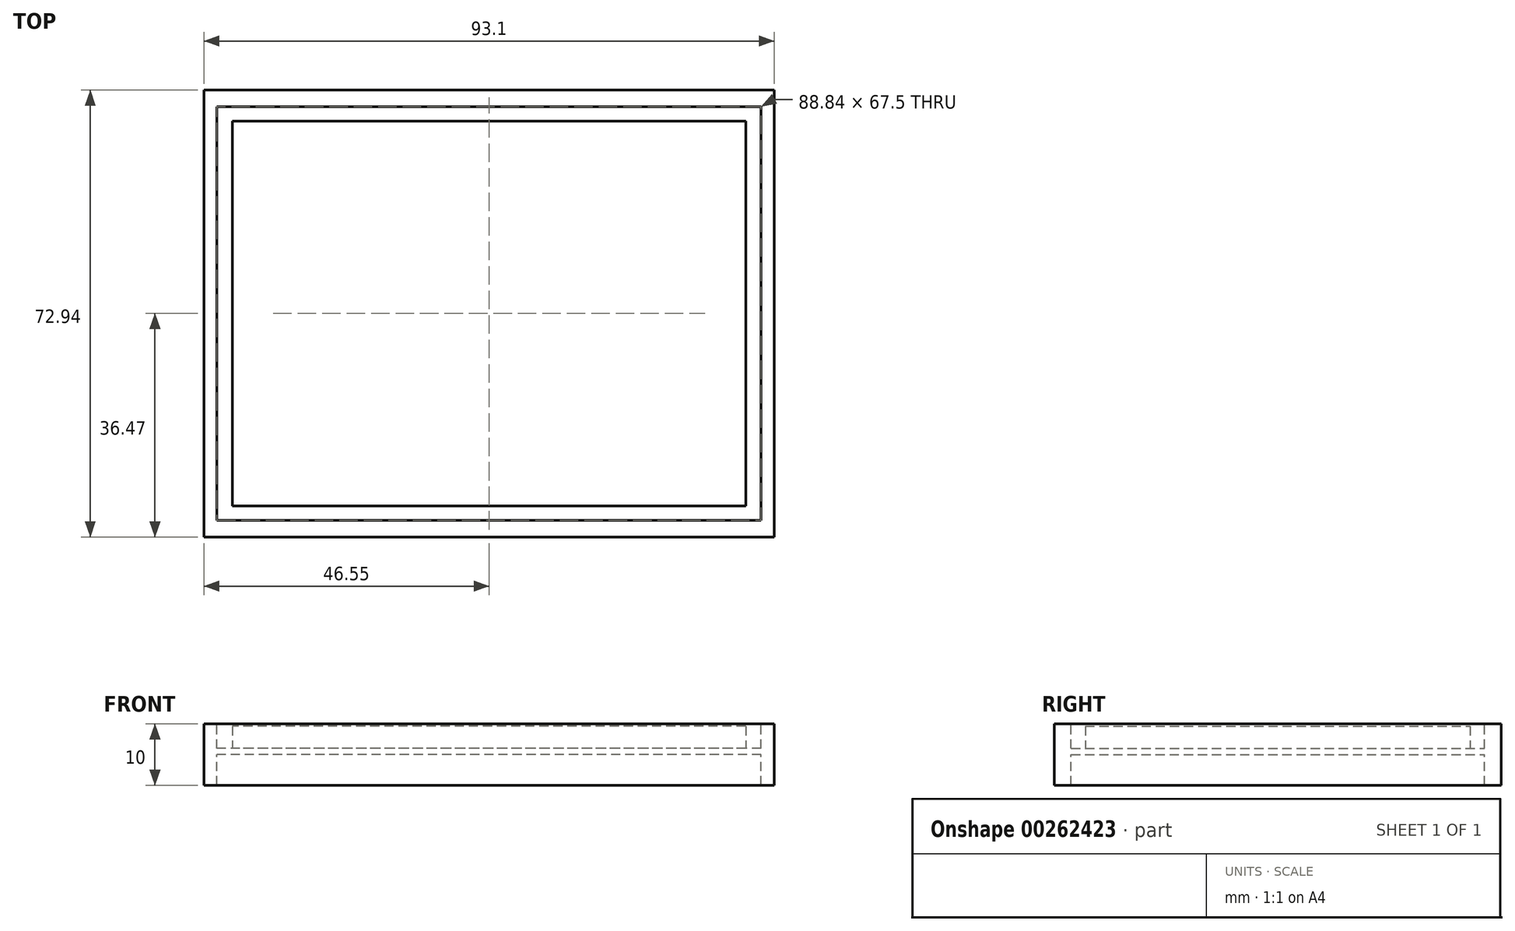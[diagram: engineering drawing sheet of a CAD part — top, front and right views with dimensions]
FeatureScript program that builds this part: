
annotation { "Feature Type Name" : "Feature", "Feature Type Description" : "" }
export const myFeature = defineFeature(function(context is Context, id is Id, definition is map)
    precondition{}
    {
        {
            var Q0;
            Q0=qCreatedBy(makeId("Top.planeOp"),FACE);
            var sketch = newSketch(context, id + "F0", { "sketchPlane" : qUnion([Q0])});
            skLineSegment(sketch, "E0.bottom", {"start": v(46.55, 36.47) * mm, "end": v(-46.55, 36.47) * mm});
            skLineSegment(sketch, "E0.top", {"start": v(46.55, -36.47) * mm, "end": v(-46.55, -36.47) * mm});
            skLineSegment(sketch, "E0.left", {"start": v(46.55, 36.47) * mm, "end": v(46.55, -36.47) * mm});
            skLineSegment(sketch, "E0.right", {"start": v(-46.55, 36.47) * mm, "end": v(-46.55, -36.47) * mm});
            skPoint(sketch, "E0.middle", {"position": v(0, 0) * mm});
            skLineSegment(sketch, "E1.bottom", {"start": v(41.9, -31.42) * mm, "end": v(-41.9, -31.42) * mm});
            skLineSegment(sketch, "E1.top", {"start": v(41.9, 31.42) * mm, "end": v(-41.9, 31.42) * mm});
            skLineSegment(sketch, "E1.left", {"start": v(41.9, -31.42) * mm, "end": v(41.9, 31.42) * mm});
            skLineSegment(sketch, "E1.right", {"start": v(-41.9, -31.42) * mm, "end": v(-41.9, 31.42) * mm});
            skLineSegment(sketch, "E2.bottom", {"start": v(44.42, -33.75) * mm, "end": v(-44.42, -33.75) * mm});
            skLineSegment(sketch, "E2.top", {"start": v(44.42, 33.75) * mm, "end": v(-44.42, 33.75) * mm});
            skLineSegment(sketch, "E2.left", {"start": v(44.42, -33.75) * mm, "end": v(44.42, 33.75) * mm});
            skLineSegment(sketch, "E2.right", {"start": v(-44.42, -33.75) * mm, "end": v(-44.42, 33.75) * mm});
            skSolve(sketch);
        }
        {
            var Q0;
            Q0 = qSketchRegion(id + "F0", true);
            extrude(context, id + "F1", {"entities" : qUnion([Q0]), "endBound" : BoundingType.SYMMETRIC, "oppositeDirection" : true, "depth" : 10 * mm});
        }
        {
            var Q0;
            Q0=makeQuery(id+"F0.imprint","IMPRINT",FACE,{"disambiguationData":[TD([[makeQuery(id+"F0.imprint","IMPRINT",EDGE,{"derivedFrom":sQuery(id+"F0.wireOp",EDGE,"E1.bottom")}),1.0]])]});
            extrude(context, id + "F2", {"entities" : qUnion([Q0]), "operationType" : NewBodyOperationType.ADD, "depth" : 1 * mm});
        }
        {
            var Q0;
            Q0=makeQuery(id+"F0.imprint","IMPRINT",FACE,{"disambiguationData":[TD([[makeQuery(id+"F0.imprint","IMPRINT",EDGE,{"derivedFrom":sQuery(id+"F0.wireOp",EDGE,"E1.bottom")}),-1.0]])]});
            extrude(context, id + "F3", {"entities" : qUnion([Q0]), "operationType" : NewBodyOperationType.ADD, "depth" : 4.6 * mm});
        }
    });
